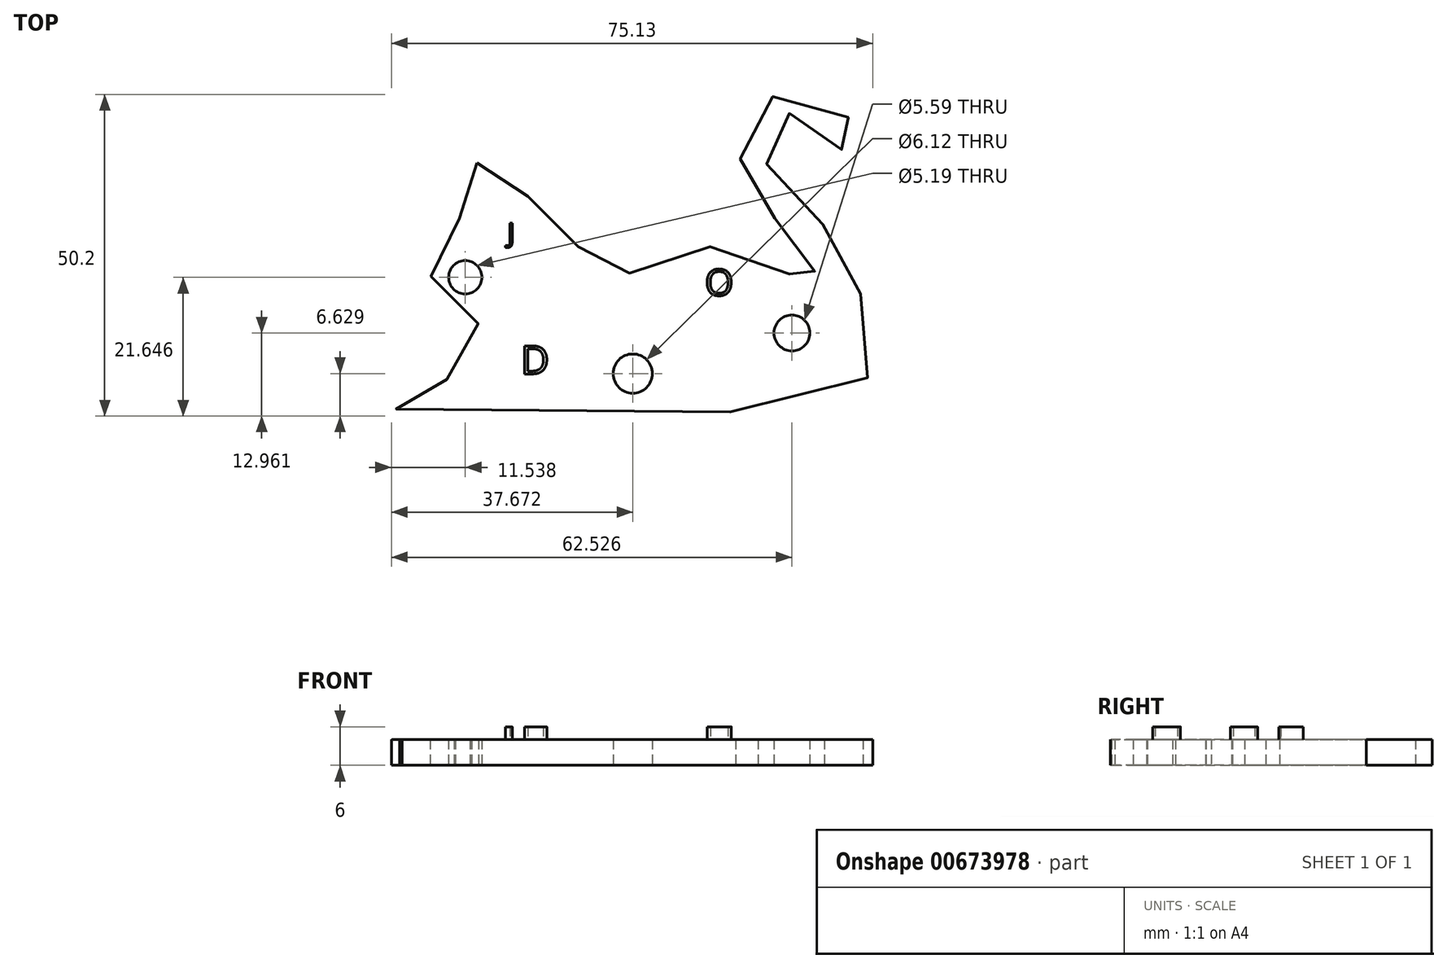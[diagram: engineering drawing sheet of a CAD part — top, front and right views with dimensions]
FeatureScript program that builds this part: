
annotation { "Feature Type Name" : "Feature", "Feature Type Description" : "" }
export const myFeature = defineFeature(function(context is Context, id is Id, definition is map)
    precondition{}
    {
        {
            var Q0;
            Q0=qCreatedBy(makeId("Top.planeOp"),FACE);
            var sketch = newSketch(context, id + "F0", { "sketchPlane" : qUnion([Q0])});
            skFitSpline(sketch, "E0", {"points": [v(13.07, -11.52) * mm, v(14.1, -12.09) * mm, v(15.34, -12.88) * mm, v(16.02, -13.67) * mm, v(16.82, -14.36) * mm, v(17.95, -15.04) * mm, v(20, -16.17) * mm, v(22.27, -17.3) * mm, v(23.85, -18.21) * mm, v(25.56, -19.46) * mm, v(26.8, -21.28) * mm, v(28.17, -23.1) * mm, v(29.19, -25.25) * mm, v(30.32, -26.95) * mm, v(31.46, -28.65) * mm, v(32.82, -29.68) * mm, v(34.63, -30.02) * mm, v(36.56, -28.88) * mm, v(39.51, -27.52) * mm, v(41.78, -26.61) * mm, v(44.73, -25.59) * mm, v(47.57, -24.8) * mm, v(50.52, -24.57) * mm, v(53.7, -25.14) * mm, v(56.2, -26.04) * mm, v(59.03, -27.3) * mm, v(61.53, -28.65) * mm, v(63.46, -29.9) * mm, v(65.16, -30.92) * mm, v(66.75, -32.06) * mm, v(67.32, -31.83) * mm, v(66.75, -30.47) * mm, v(65.96, -28.77) * mm, v(65.05, -26.84) * mm, v(63.69, -25.14) * mm, v(63, -24.23) * mm, v(61.87, -22.98) * mm, v(60.62, -21.4) * mm, v(59.6, -20.14) * mm, v(58.35, -18.44) * mm, v(57.33, -17.3) * mm, v(56.2, -15.5) * mm, v(55.29, -13.9) * mm, v(54.5, -12.09) * mm, v(53.93, -9.82) * mm, v(53.47, -7.43) * mm, v(54.15, -4.6) * mm, v(55.74, -2.55) * mm, v(58.47, -1.3) * mm, v(61.76, -0.85) * mm, v(64.93, -0.85) * mm, v(67.43, -1.3) * mm, v(69.59, -2.55) * mm, v(71.29, -4.82) * mm, v(72.42, -6.98) * mm, v(73.33, -9.25) * mm, v(73, -10.5) * mm, v(71.97, -11.06) * mm, v(70.38, -10.27) * mm, v(69.81, -8.8) * mm, v(68.57, -6.53) * mm, v(67.43, -4.7) * mm, v(65.39, -3.46) * mm, v(63.23, -3.57) * mm, v(61.76, -3.8) * mm, v(60.05, -4.6) * mm, v(58.8, -5.28) * mm, v(57.56, -6.53) * mm, v(57, -8.9) * mm, v(57.67, -10.84) * mm, v(58.92, -12.31) * mm, v(60.85, -14.24) * mm, v(62.44, -15.83) * mm, v(64.03, -17.42) * mm, v(66.52, -20.48) * mm, v(68.11, -22.41) * mm, v(69.36, -24.8) * mm, v(70.27, -26.61) * mm, v(71.4, -29) * mm, v(72.76, -31.6) * mm, v(73.79, -33.76) * mm, v(74.78, -36.82) * mm, v(74.78, -39.43) * mm, v(74.78, -42.27) * mm, v(73.33, -46.7) * mm, v(72.08, -49.2) * mm, v(71.18, -50.77) * mm, v(67.77, -50.77) * mm, v(1.04, -50.77) * mm, v(1.38, -50.77) * mm, v(0, -49.42) * mm, v(0, -47.83) * mm, v(1.61, -46.7) * mm, v(3.65, -45.68) * mm, v(5.7, -45.45) * mm, v(8.08, -45.22) * mm, v(9.56, -45.22) * mm, v(9.56, -42.73) * mm, v(10.24, -40.23) * mm, v(12.28, -37.85) * mm, v(13.19, -37.4) * mm, v(13.07, -36.26) * mm, v(11.26, -36.14) * mm, v(9.21, -35) * mm, v(6.5, -33.2) * mm, v(5.81, -31.26) * mm, v(6.04, -29) * mm, v(6.95, -28.43) * mm, v(7.29, -27.18) * mm, v(7.51, -25.59) * mm, v(8.08, -23.55) * mm, v(9.21, -21.5) * mm, v(11.03, -19.58) * mm, v(12.28, -18.67) * mm, v(12.05, -18.44) * mm, v(12.05, -17.2) * mm, v(11.94, -14.36) * mm, v(12.05, -12.09) * mm, v(13.07, -11.52) * mm]});
            skLineSegment(sketch, "E1", {"start": v(64.93, -0.85) * mm, "end": v(67.77, -50.77) * mm, "construction": true});
            skCircle(sketch, "E2", {"center": v(37.4, -44.37) * mm, "radius": 3.06 * mm});
            skCircle(sketch, "E3", {"center": v(62.25, -38.04) * mm, "radius": 2.8 * mm});
            skCircle(sketch, "E4", {"center": v(11.26, -29.35) * mm, "radius": 2.6 * mm});
            skSolve(sketch);
        }
        {
            var Q0;
            Q0=makeQuery(id+"F0.imprint","IMPRINT",FACE,{"disambiguationData":[TD([[makeQuery(id+"F0.imprint","IMPRINT",EDGE,{"derivedFrom":sQuery(id+"F0.wireOp",EDGE,"E0")}),-1.0]])]});
            extrude(context, id + "F1", {"entities" : qUnion([Q0]), "depth" : 4 * mm, "offsetDistance" : 25 * mm});
        }
        {
            var Q0;
            Q0=makeQuery(id+"F1.opExtrude","CAP_FACE",FACE,{"disambiguationData":[OSD([sQuery(id+"F0.wireOp",EDGE,"E0")])],"isStart":false});
            var sketch = newSketch(context, id + "F2", { "sketchPlane" : qUnion([Q0])});
            skText(sketch, "E5", { "text": "J", "fontName": "OpenSans-Regular.ttf"});
            const initialGuessF2  = {"E5": [0.01784, -0.02393, 1, 0, 0.00303]};
            skSetInitialGuess(sketch, initialGuessF2);
            skSolve(sketch);
        }
        {
            var Q0;
            Q0 = qSketchRegion(id + "F2", true);
            extrude(context, id + "F3", {"entities" : qUnion([Q0]), "operationType" : NewBodyOperationType.ADD, "depth" : 2 * mm, "offsetDistance" : 25 * mm});
        }
        {
            var Q0;
            {var subQ0=sQuery(id+"F0.wireOp",EDGE,"E0");Q0=makeQuery(id+"FG2di0vLe9BkhvU_1.boolean.opBoolean","SPLIT",FACE,{"disambiguationData":[TD([makeQuery(id+"F1.opExtrude","SWEPT_FACE",FACE,{"disambiguationData":[OSD([subQ0])]})])],"derivedFrom":makeQuery(id+"F1.opExtrude","CAP_FACE",FACE,{"disambiguationData":[OSD([subQ0])],"isStart":false})});}
            var sketch = newSketch(context, id + "F4", { "sketchPlane" : qUnion([Q0])});
            skText(sketch, "E6", { "text": "D", "fontName": "OpenSans-Regular.ttf"});
            const initialGuessF4  = {"E6": [0.0199, -0.04443, 1, 0, 0.0044]};
            skSetInitialGuess(sketch, initialGuessF4);
            skSolve(sketch);
        }
        {
            var Q0;
            Q0 = qSketchRegion(id + "F4", true);
            extrude(context, id + "F5", {"entities" : qUnion([Q0]), "operationType" : NewBodyOperationType.ADD, "depth" : 2 * mm, "offsetDistance" : 25 * mm});
        }
        {
            var Q0;
            {var subQ0=sQuery(id+"F0.wireOp",EDGE,"E0");var subQ1=sQuery(id+"F0.wireOp",EDGE,"E2");var subQ2=sQuery(id+"F0.wireOp",EDGE,"E3");Q0=makeQuery(id+"F5.boolean.opBoolean","SPLIT",FACE,{"disambiguationData":[TD([makeQuery(id+"F1.opExtrude","SWEPT_FACE",FACE,{"disambiguationData":[OSD([subQ0])]})])],"derivedFrom":makeQuery(id+"F1.opExtrude","CAP_FACE",FACE,{"disambiguationData":[OSD([subQ0,subQ1,subQ2])],"isStart":false})});}
            var sketch = newSketch(context, id + "F6", { "sketchPlane" : qUnion([Q0])});
            skText(sketch, "E7", { "text": "O", "fontName": "OpenSans-Regular.ttf"});
            const initialGuessF6  = {"E7": [0.04865, -0.0322, 1, 0, 0.00413]};
            skSetInitialGuess(sketch, initialGuessF6);
            skSolve(sketch);
        }
        {
            var Q0;
            Q0 = qSketchRegion(id + "F6", true);
            extrude(context, id + "F7", {"entities" : qUnion([Q0]), "operationType" : NewBodyOperationType.ADD, "depth" : 2 * mm, "offsetDistance" : 25 * mm});
        }
    });
